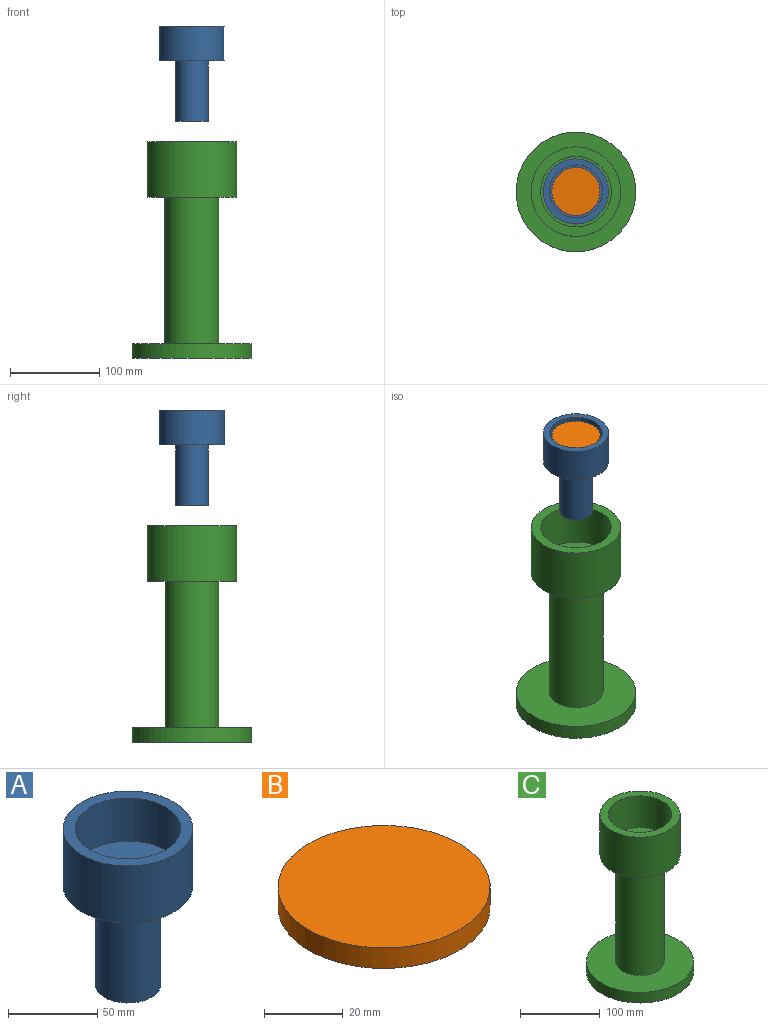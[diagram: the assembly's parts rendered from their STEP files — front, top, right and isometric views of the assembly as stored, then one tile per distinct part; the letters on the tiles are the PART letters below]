
ASSEMBLY  parts=3 mates=2
PART A: 8 faces, bbox 72.9x72.9x106.9 mm
  f0: plane 59.24x59.24mm, normal (0,0,1), area 2489.7mm2, adj f1,f7
  f1: cylinder r=9.22mm len=77.27mm, axis (0,0,-1), area 4475.1mm2, adj f0,f2
  f2: plane 36.87x36.87mm, normal (0,0,-1), area 800.8mm2, adj f1,f3
  f3: cylinder r=18.44mm len=67.74mm, axis (0,0,-1), area 7846.5mm2, adj f2,f4
  f4: plane 72.92x72.92mm, normal (0,0,-1), area 3107.9mm2, adj f3,f5
  f5: cylinder r=36.46mm len=72.92mm, axis (0,0,-1), area 8968.3mm2, adj f4,f6
  f6: plane 72.92x72.92mm, normal (0,0,1), area 1419.1mm2, adj f5,f7
  f7: cylinder r=29.62mm len=59.24mm, axis (0,0,-1), area 5513.3mm2, adj f0,f6
PART B: 3 faces, bbox 53.8x53.8x6.4 mm
  f0: cylinder r=26.89mm len=53.78mm, axis (0,0,-1), area 1072.9mm2, adj f1,f2
  f1: plane 53.78x53.78mm, normal (0,0,1), area 2271.6mm2, adj f0
  f2: plane 53.78x53.78mm, normal (0,0,-1), area 2271.6mm2, adj f0
PART C: 11 faces, bbox 134x134x242 mm
  f0: cylinder r=39.57mm len=79.13mm, axis (0,0,1), area 12030.9mm2, adj f1,f10
  f1: plane 100.26x100.26mm, normal (0,0,1), area 2976.9mm2, adj f0,f2
  f2: cylinder r=50.13mm len=100.26mm, axis (0,0,1), area 19573.7mm2, adj f1,f3
  f3: plane 100.26x100.26mm, normal (0,0,-1), area 5021.2mm2, adj f2,f4
  f4: cylinder r=30.24mm len=163.66mm, axis (0,0,1), area 31100.2mm2, adj f3,f5
  f5: plane 133.98x133.98mm, normal (0,0,1), area 11223.9mm2, adj f4,f6
  f6: cylinder r=66.99mm len=133.98mm, axis (0,0,1), area 6809.3mm2, adj f5,f7
  f7: plane 133.98x133.98mm, normal (0,0,-1), area 14097.4mm2, adj f6
  f8: plane 40.37x40.37mm, normal (0,0,1), area 1280mm2, adj f9
  f9: cylinder r=20.19mm len=177.41mm, axis (0,0,1), area 22500.7mm2, adj f8,f10
  f10: plane 79.13x79.13mm, normal (0,0,1), area 3637.8mm2, adj f0,f9
PLACE A t=(4.93,3.55,136.2)mm
PLACE B t=(4.93,3.55,165.72)mm
PLACE C t=(4.93,3.55,0)mm fixed
MATE slider C.f0 <-> B.f0  axis (0,0,1) through (4.93,3.55,-2.82)mm
MATE slider A.f1 <-> C.f0  axis (0,0,-1) through (4.93,3.55,68.47)mm
